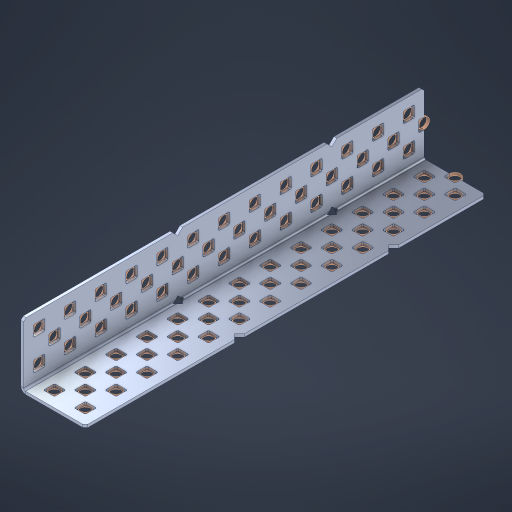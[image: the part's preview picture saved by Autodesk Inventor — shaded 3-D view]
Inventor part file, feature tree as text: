
AUTODESK INVENTOR PART (.ipt)
format: ipt  version: 2023 (Build 270158000, 158)  size: 1,135,104 bytes
history: native  units: in
note: dims shown in document units (in); Inventor stores cm internally (conversion verified against a paired STEP export)
features: other x84, extrude x76, sheet_metal_op x8, sketch x7, pattern_linear x2, mirror x1, chamfer x1
ambient origin geometry x8: Origin, YZ Plane, XZ Plane, XY Plane, X Axis, Y Axis, Z Axis, Center Point
bodies: Solid1 (feature_tree), Body (feature_tree)
feature tree (179):
  sheet_metal_op  "Flanges"
  sheet_metal_op  "Body Pattern"
  pattern_linear  "Center Pattern"  Spacing1=1.0in  [1 undecoded]
  other  "Arc Length"
  pattern_linear  "Notch Pattern"  Spacing1=0.1875in  [1 undecoded]
  other  "Diagonal Plane"
  mirror  "Everything Mirrored"
  chamfer  "End Chamfer"
  sketch  "Sketch1"  dims[d0=1.0in]
  other  "Plate1"
  sketch  "Sketch2"  dims[d1=6.5in]
  other  "Plate2"
  sheet_metal_op  "Bend1"
  sheet_metal_op  "Corner1"
  sketch  "Sketch8"  dims[d2=0.0469in]
  sketch  "Sketch9"  dims[d3=0.0469in]
  other  "Srf91"
  sheet_metal_op  "Body Pattern Sketch"
  other  "Srf92"
  sketch  "Sketch13"  dims[d4=0.0234in]
  sketch  "Sketch15"  dims[d5=0.0938in]
  sketch  "Sketch16"  dims[d6=0.0469in d7=1.0in d8=90.0deg d9=0.0312in d10=0.1875in d11=0.0469in d12=0.0469in d49=0.182in d50=0.02in d52=0.25in d53=0.0469in d54=0.0in d55=0.172in d56=1.0in d57=0.0in d60=5.1181in d62=0.5in d63=0.7874in d65=0.5in d85=0.1473in d86=0.1659in d89=0.0469in d90=0.0in d91=0.04in d92=0.0491in d95=2.5in d96=0.04in d97=0.25in d98=45.0deg d99=0.25in d106=0.182in d107=0.02in d108=0.5in d110=0.0469in d111=0.0in d112=0.172in d113=0.5in d114=0.0in d117=0.5in d123=0.25in d125=0.25in d126=0.0491in d127=0.1227in d128=0.08in d129=0.04in d130=2.5in]
  other  "Srf786"
  other  "Srf856"
  other  "Srf857"
  other  "Srf858"
  other  "Srf859"
  other  "Srf860"
  other  "Srf861"
  other  "Srf889"
  other  "Srf890"
  other  "Srf891"
  other  "Srf1275"
  other  "Srf1276"
  other  "Srf1278"
  other  "Srf1279"
  other  "Srf1280"
  other  "Srf1281"
  other  "Srf1282"
  other  "Srf1283"
  other  "Srf1277"
  other  "Srf1285"
  other  "Srf1286"
  other  "Srf1287"
  other  "Srf1383"
  other  "Srf1384"
  other  "Srf1385"
  other  "Srf1386"
  other  "Srf1387"
  other  "Srf1388"
  other  "Srf1389"
  other  "Srf1390"
  other  "Srf1391"
  other  "Srf1392"
  other  "Srf1393"
  other  "Srf1394"
  other  "Srf1395"
  other  "Srf1396"
  other  "Srf1397"
  other  "Srf1398"
  other  "Srf1399"
  other  "Srf1400"
  other  "Srf1445"
  other  "Srf1446"
  other  "Srf1447"
  other  "Srf1448"
  other  "Srf1449"
  other  "Srf1450"
  other  "Srf1451"
  other  "Srf1452"
  other  "Srf1453"
  other  "Srf1475"
  other  "Srf1476"
  other  "Srf1477"
  other  "Srf1478"
  other  "Srf1479"
  other  "Srf1480"
  other  "Srf1481"
  other  "Srf1482"
  other  "Srf1483"
  other  "Srf1484"
  other  "Srf1485"
  other  "Srf1486"
  other  "Srf1487"
  other  "Srf1488"
  other  "Srf1489"
  other  "Srf1490"
  other  "Srf1491"
  other  "Srf1492"
  other  "Srf1537"
  other  "Srf1538"
  other  "Srf1539"
  other  "Srf1540"
  other  "Srf1541"
  other  "Srf1542"
  other  "Srf1543"
  other  "Srf1544"
  other  "Srf1545"
  sheet_metal_op  "Body Stamp"
  sheet_metal_op  "Body Circle"
  other  "Center Stamp"
  other  "Center Circle"
  sheet_metal_op  "Notch"
  extrude  "ExtrusionSrf92"  Depth=0.0469in
  extrude  "ExtrusionSrf856"  Depth=0.0469in
  extrude  "ExtrusionSrf857"  Depth=0.182in
  extrude  "ExtrusionSrf858"  Depth=0.02in
  extrude  "ExtrusionSrf859"  Depth=0.25in
  extrude  "ExtrusionSrf860"  Depth=0.0469in
  extrude  "ExtrusionSrf861"  TaperAngle=0.0deg  [1 undecoded]
  extrude  "ExtrusionSrf889"  Depth=2.5in
  extrude  "ExtrusionSrf890"  Depth=1.0in TaperAngle=0.0deg
  extrude  "ExtrusionSrf891"  Depth=2.5in
  extrude  "ExtrusionSrf1275"  Depth=0.5in
  extrude  "ExtrusionSrf1276"  Depth=2.5in
  extrude  "ExtrusionSrf1277"  Depth=2.5in
  extrude  "ExtrusionSrf1278"  Depth=0.0469in
  extrude  "ExtrusionSrf1279"  Depth=2.5in TaperAngle=0.0deg
  extrude  "ExtrusionSrf1280"  Depth=2.5in
  extrude  "ExtrusionSrf1281"  Depth=0.25in TaperAngle=45.0deg
  extrude  "ExtrusionSrf1282"  Depth=0.25in
  extrude  "ExtrusionSrf1345"  Depth=0.182in
  extrude  "ExtrusionSrf1346"  Depth=0.02in
  extrude  "ExtrusionSrf1347"  Depth=0.5in
  extrude  "ExtrusionSrf1348"  Depth=0.0469in
  extrude  "ExtrusionSrf1383"  TaperAngle=0.0deg  [1 undecoded]
  extrude  "ExtrusionSrf1384"  Depth=2.5in
  extrude  "ExtrusionSrf1385"  Depth=0.5in TaperAngle=0.0deg
  extrude  "ExtrusionSrf1386"  Depth=0.5in
  extrude  "ExtrusionSrf1387"  Depth=0.25in
  extrude  "ExtrusionSrf1388"  Depth=0.25in
  extrude  "ExtrusionSrf1389"  Depth=2.5in
  extrude  "ExtrusionSrf1390"  Depth=2.5in
  extrude  "ExtrusionSrf1391"  Depth=2.5in
  extrude  "ExtrusionSrf1392"  Depth=2.5in
  extrude  "ExtrusionSrf1393"  Depth=2.5in
  extrude  "ExtrusionSrf1394"  [1 undecoded]
  extrude  "ExtrusionSrf1395"  [1 undecoded]
  extrude  "ExtrusionSrf1396"  [1 undecoded]
  extrude  "ExtrusionSrf1397"  [1 undecoded]
  extrude  "ExtrusionSrf1398"  [1 undecoded]
  extrude  "ExtrusionSrf1399"  [1 undecoded]
  extrude  "ExtrusionSrf1400"  [1 undecoded]
  extrude  "ExtrusionSrf1445"  [1 undecoded]
  extrude  "ExtrusionSrf1446"  [1 undecoded]
  extrude  "ExtrusionSrf1447"  [1 undecoded]
  extrude  "ExtrusionSrf1448"  [1 undecoded]
  extrude  "ExtrusionSrf1449"  [1 undecoded]
  extrude  "ExtrusionSrf1450"  [1 undecoded]
  extrude  "ExtrusionSrf1451"  [1 undecoded]
  extrude  "ExtrusionSrf1452"  [1 undecoded]
  extrude  "ExtrusionSrf1453"  [1 undecoded]
  extrude  "ExtrusionSrf1475"  [1 undecoded]
  extrude  "ExtrusionSrf1476"  [1 undecoded]
  extrude  "ExtrusionSrf1477"  [1 undecoded]
  extrude  "ExtrusionSrf1478"  [1 undecoded]
  extrude  "ExtrusionSrf1479"  [1 undecoded]
  extrude  "ExtrusionSrf1480"  [1 undecoded]
  extrude  "ExtrusionSrf1481"  [1 undecoded]
  extrude  "ExtrusionSrf1482"  [1 undecoded]
  extrude  "ExtrusionSrf1483"  [1 undecoded]
  extrude  "ExtrusionSrf1484"  [1 undecoded]
  extrude  "ExtrusionSrf1485"  [1 undecoded]
  extrude  "ExtrusionSrf1486"  [1 undecoded]
  extrude  "ExtrusionSrf1487"  [1 undecoded]
  extrude  "ExtrusionSrf1488"  [1 undecoded]
  extrude  "ExtrusionSrf1489"  [1 undecoded]
  extrude  "ExtrusionSrf1490"  [1 undecoded]
  extrude  "ExtrusionSrf1491"  [1 undecoded]
  extrude  "ExtrusionSrf1492"  [1 undecoded]
  extrude  "ExtrusionSrf1537"  [1 undecoded]
  extrude  "ExtrusionSrf1538"  [1 undecoded]
  extrude  "ExtrusionSrf1539"  [1 undecoded]
  extrude  "ExtrusionSrf1540"  [1 undecoded]
  extrude  "ExtrusionSrf1541"  [1 undecoded]
  extrude  "ExtrusionSrf1542"  [1 undecoded]
  extrude  "ExtrusionSrf1543"  [1 undecoded]
  extrude  "ExtrusionSrf1544"  [1 undecoded]
  extrude  "ExtrusionSrf1545"  [1 undecoded]
note: 47 required parameter values undecoded (feature->parameter linkage not recoverable at this tier; creation-order binding heuristic only, values carry confidence <= 0.55)
